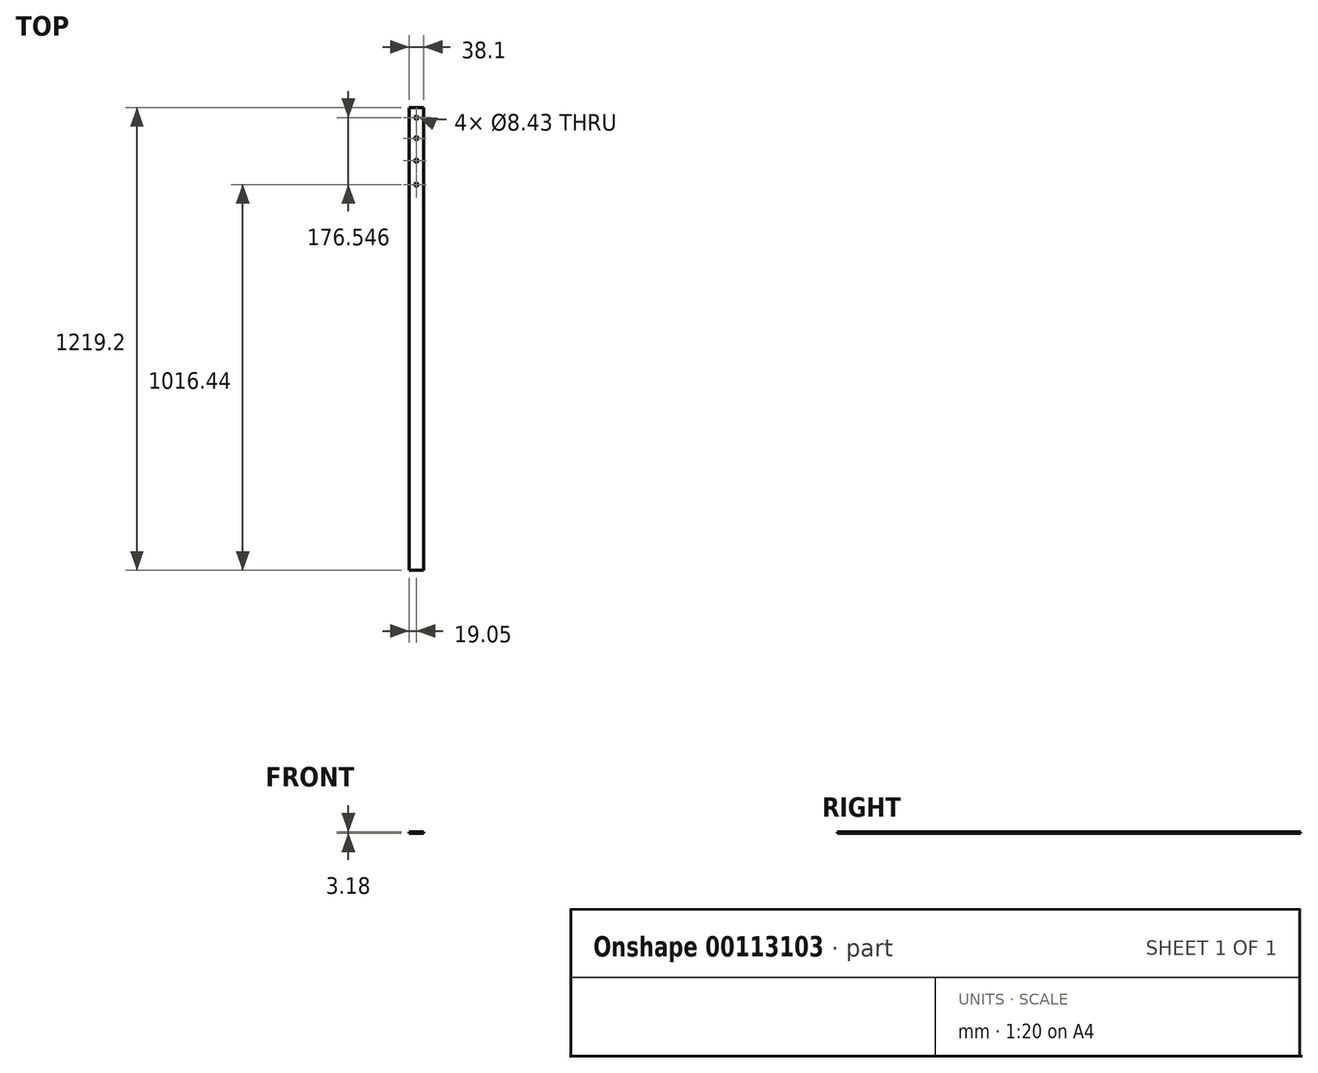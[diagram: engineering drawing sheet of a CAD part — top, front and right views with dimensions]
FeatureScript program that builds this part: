
annotation { "Feature Type Name" : "Feature", "Feature Type Description" : "" }
export const myFeature = defineFeature(function(context is Context, id is Id, definition is map)
    precondition{}
    {
        {
            var Q0;
            Q0=qCreatedBy(makeId("Front.planeOp"),FACE);
            var sketch = newSketch(context, id + "F0", { "sketchPlane" : qUnion([Q0])});
            skLineSegment(sketch, "E0.bottom", {"start": v(19.05, -1.59) * mm, "end": v(-19.05, -1.59) * mm});
            skLineSegment(sketch, "E0.top", {"start": v(19.05, 1.59) * mm, "end": v(-19.05, 1.59) * mm});
            skLineSegment(sketch, "E0.left", {"start": v(19.05, -1.59) * mm, "end": v(19.05, 1.59) * mm});
            skLineSegment(sketch, "E0.right", {"start": v(-19.05, -1.59) * mm, "end": v(-19.05, 1.59) * mm});
            skPoint(sketch, "E0.middle", {"position": v(0, 0) * mm});
            skLineSegment(sketch, "E1.bottom", {"start": v(-19.05, 1.59) * mm, "end": v(-15.87, 1.59) * mm});
            skLineSegment(sketch, "E1.top", {"start": v(-19.05, 26.99) * mm, "end": v(-15.88, 26.99) * mm});
            skLineSegment(sketch, "E1.left", {"start": v(-19.05, 1.59) * mm, "end": v(-19.05, 26.99) * mm});
            skLineSegment(sketch, "E1.right", {"start": v(-15.87, 1.59) * mm, "end": v(-15.88, 26.99) * mm});
            skLineSegment(sketch, "E2.bottom", {"start": v(19.05, 1.59) * mm, "end": v(15.88, 1.59) * mm});
            skLineSegment(sketch, "E2.top", {"start": v(19.05, 26.99) * mm, "end": v(15.87, 26.99) * mm});
            skLineSegment(sketch, "E2.left", {"start": v(19.05, 1.59) * mm, "end": v(19.05, 26.99) * mm});
            skLineSegment(sketch, "E2.right", {"start": v(15.88, 1.59) * mm, "end": v(15.87, 26.99) * mm});
            skSolve(sketch);
        }
        {
            var Q0;
            Q0=makeQuery(id+"F0.imprint","IMPRINT",FACE,{"disambiguationData":[TD([[makeQuery(id+"F0.imprint","IMPRINT",EDGE,{"derivedFrom":sQuery(id+"F0.wireOp",EDGE,"E1.bottom")}),1.0]])]});
            var Q1;
            Q1=makeQuery(id+"F0.imprint","IMPRINT",FACE,{"disambiguationData":[TD([[makeQuery(id+"F0.imprint","IMPRINT",EDGE,{"derivedFrom":sQuery(id+"F0.wireOp",EDGE,"E2.bottom")}),-1.0]])]});
            var Q2;
            Q2=makeQuery(id+"F0.imprint","IMPRINT",FACE,{"disambiguationData":[TD([[makeQuery(id+"F0.imprint","IMPRINT",EDGE,{"derivedFrom":sQuery(id+"F0.wireOp",EDGE,"E0.bottom")}),-1.0]])]});
            extrude(context, id + "F1", {"entities" : qUnion([Q0, Q1, Q2]), "depth" : 1219.2 * mm});
        }
        {
            var Q0;
            Q0=makeQuery(id+"F1.opExtrude","SWEPT_FACE",FACE,{"disambiguationData":[OSD([sQuery(id+"F0.wireOp",EDGE,"E0.top")])]});
            var sketch = newSketch(context, id + "F2", { "sketchPlane" : qUnion([Q0])});
            skPoint(sketch, "E3", {"position": v(0, -26.22) * mm});
            skPoint(sketch, "E4", {"position": v(0, -80.68) * mm});
            skPoint(sketch, "E5", {"position": v(0, -140.13) * mm});
            skPoint(sketch, "E6", {"position": v(0, -202.76) * mm});
            skSolve(sketch);
        }
        {
            var Q0;
            Q0=sQuery(id+"F2.wireOp",VERTEX,"E3");
            var Q1;
            Q1=sQuery(id+"F2.wireOp",VERTEX,"E4");
            var Q2;
            Q2=sQuery(id+"F2.wireOp",VERTEX,"E5");
            var Q3;
            Q3=sQuery(id+"F2.wireOp",VERTEX,"E6");
            var Q4;
            Q4=makeQuery(id+"F1.opExtrude","SWEPT_BODY",BODY,{"disambiguationData":[OSD([sQuery(id+"F0.wireOp",EDGE,"E0.bottom"),sQuery(id+"F0.wireOp",EDGE,"E0.top"),sQuery(id+"F0.wireOp",EDGE,"E0.left"),sQuery(id+"F0.wireOp",EDGE,"E0.right"),sQuery(id+"F0.wireOp",EDGE,"E1.top"),sQuery(id+"F0.wireOp",EDGE,"E1.left"),sQuery(id+"F0.wireOp",EDGE,"E1.right"),sQuery(id+"F0.wireOp",EDGE,"E2.top"),sQuery(id+"F0.wireOp",EDGE,"E2.left"),sQuery(id+"F0.wireOp",EDGE,"E2.right")])]});
            hole(context, id + "F3", {"style" : HoleStyle.SIMPLE, "endStyle" : HoleEndStyle.THROUGH, "standardTappedOrClearance" : lookupTablePath({ "standard" : "ANSI", "fit" : "Normal (ASME)", "size" : "5/16", "type" : "Clearance" }), "standardBlindInLast" : lookupTablePath({ "fit" : "Free", "standard" : "ANSI", "size" : "5/16", "type" : "Clearance" }), "holeDiameter" : 8.43 * mm, "locations" : qUnion([Q0, Q1, Q2, Q3]), "scope" : qUnion([Q4]), "isTappedThrough" : true, "startStyle" : HoleStartStyle.SKETCH});
        }
    });
